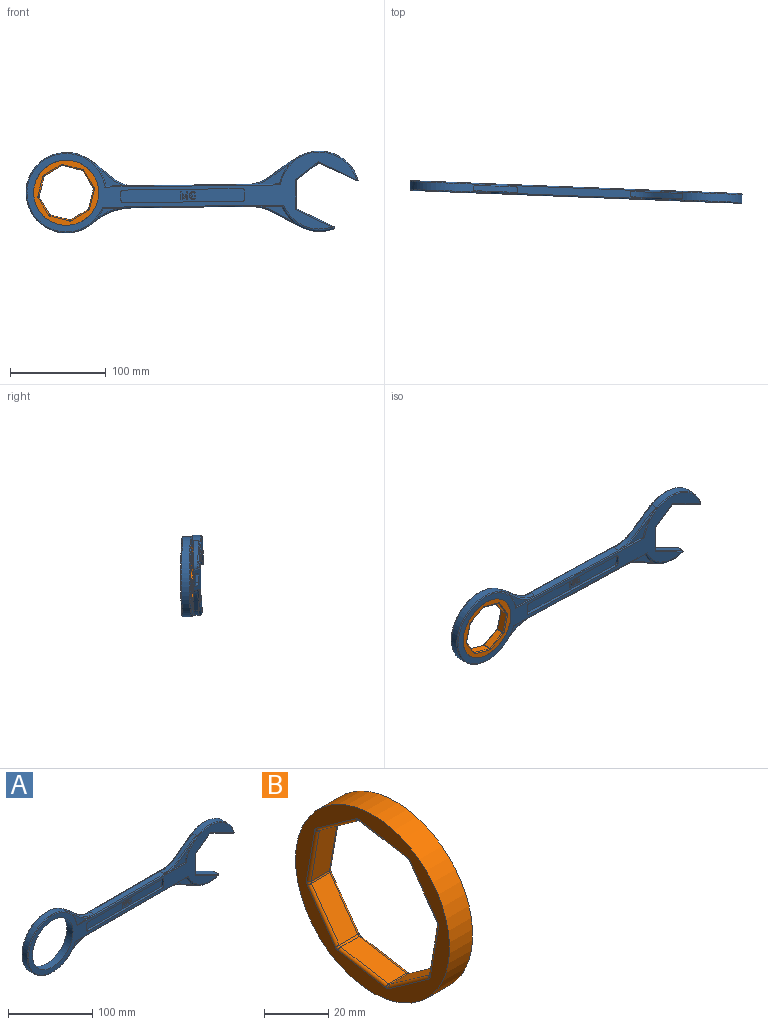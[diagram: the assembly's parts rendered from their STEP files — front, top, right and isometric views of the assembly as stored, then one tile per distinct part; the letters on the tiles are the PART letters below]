
ASSEMBLY  parts=2 mates=1
PART A: 202 faces, bbox 353.1x10.8x92.8 mm
  f0: plane 146.75x8.45mm, normal (0,0,-1), area 986mm2, adj f6,f9,f10,f187,f190,f191,f194,f196
  f1: plane 1.62x0.64mm, normal (0,0,-1), area 0.3mm2, adj f5,f162,f196
  f2: plane 1.62x0.64mm, normal (0,0,-1), area 0.3mm2, adj f4,f161,f194
  f3: plane 137.92x8.42mm, normal (0,0,1), area 976.1mm2, adj f179,f182,f183,f184,f192,f193,f195,f197
  f4: cylinder r=41.91mm len=21.18mm, axis (0,1,0), area 40.1mm2, adj f2,f6,f8,f9,f161
  f5: cylinder r=41.91mm len=21.18mm, axis (0,1,0), area 40.1mm2, adj f1,f6,f7,f10,f162
  f6: extruded ~54.46x21.18mm, area 331.4mm2, adj f0,f4,f5,f9,f10,f11
  f7: plane 34.13x16.45mm, normal (0,-1,0), area 139.1mm2, adj f5,f10,f196
  f8: plane 34.12x16.45mm, normal (0,1,0), area 139.1mm2, adj f4,f9,f194
  f9: bspline ~61.81x25.48mm, area 97mm2, adj f0,f4,f6,f8
  f10: bspline ~57.96x23.23mm, area 97mm2, adj f0,f5,f6,f7
  f11: cylinder r=41.91mm len=36.16mm, axis (0,1,0), area 190.7mm2, adj f6,f161,f162,f169
  f12: cylinder r=41.91mm len=69.07mm, axis (0,1,0), area 633.7mm2, adj f174,f175,f178,f179,f182,f183
  f13: plane 0.9x0.64mm, normal (1,0,0), area 0.6mm2, adj f14,f27,f128,f160
  f14: plane 2.67x0.64mm, normal (0,0,-1), area 1.7mm2, adj f13,f15,f128,f160
  f15: plane 3.12x0.64mm, normal (-1,0,0), area 2mm2, adj f14,f16,f128,f160
  f16: extruded ~0.64x0.56mm, area 0.5mm2, adj f15,f17,f128,f160
  f17: extruded ~0.66x0.64mm, area 0.5mm2, adj f16,f18,f128,f160
  f18: extruded ~0.71x0.64mm, area 0.5mm2, adj f17,f19,f128,f160
  f19: extruded ~0.73x0.64mm, area 0.5mm2, adj f18,f20,f128,f160
  f20: plane 0.64x0.01mm, normal (0,0,1), area 0mm2, adj f19,f21,f128,f160
  f21: plane 0.96x0.64mm, normal (1,0,0), area 0.6mm2, adj f20,f22,f128,f160
  f22: extruded ~0.64x0.32mm, area 0.2mm2, adj f21,f23,f128,f160
  f23: extruded ~0.64x0.39mm, area 0.3mm2, adj f22,f24,f128,f160
  f24: extruded ~0.64x0.38mm, area 0.3mm2, adj f23,f25,f128,f160
  f25: extruded ~0.64x0.27mm, area 0.2mm2, adj f24,f26,f128,f160
  f26: plane 1.99x0.64mm, normal (1,0,0), area 1.3mm2, adj f25,f27,f128,f160
  f27: plane 1.37x0.64mm, normal (0,0,1), area 0.9mm2, adj f13,f26,f128,f160
  f28: extruded ~1.24x0.64mm, area 0.9mm2, adj f29,f45,f128,f158
  f29: extruded ~1.67x0.64mm, area 1.1mm2, adj f28,f30,f128,f158
  f30: extruded ~1.67x0.64mm, area 1.1mm2, adj f29,f31,f128,f158
  f31: extruded ~1.24x0.64mm, area 0.9mm2, adj f30,f32,f128,f158
  f32: extruded ~0.92x0.8mm, area 0.8mm2, adj f31,f33,f128,f158
  f33: extruded ~1.16x0.64mm, area 0.8mm2, adj f32,f34,f128,f158
  f34: plane 1.09x0.64mm, normal (-1,0,0), area 0.7mm2, adj f33,f35,f128,f158
  f35: extruded ~0.64x0.61mm, area 0.4mm2, adj f34,f36,f128,f158
  f36: extruded ~0.64x0.57mm, area 0.5mm2, adj f35,f37,f128,f158
  f37: extruded ~0.89x0.64mm, area 0.6mm2, adj f36,f38,f128,f158
  f38: extruded ~1.23x0.64mm, area 0.8mm2, adj f37,f39,f128,f158
  f39: extruded ~1.25x0.64mm, area 0.8mm2, adj f38,f40,f128,f158
  f40: extruded ~0.92x0.64mm, area 0.6mm2, adj f39,f41,f128,f158
  f41: extruded ~0.64x0.62mm, area 0.5mm2, adj f40,f42,f128,f158
  f42: extruded ~0.64x0.61mm, area 0.4mm2, adj f41,f43,f128,f158
  f43: plane 1x0.64mm, normal (-1,0,0), area 0.6mm2, adj f42,f44,f128,f158
  f44: extruded ~1.16x0.64mm, area 0.8mm2, adj f43,f45,f128,f158
  f45: extruded ~0.92x0.81mm, area 0.8mm2, adj f28,f44,f128,f158
  f46: extruded ~1.02x0.66mm, area 0.8mm2, adj f47,f53,f128,f156
  f47: plane 0.91x0.81mm, normal (-0.66,0,0.75), area 0.8mm2, adj f46,f48,f128,f156
  f48: extruded ~0.64x0.6mm, area 0.5mm2, adj f47,f49,f128,f156
  f49: extruded ~0.7x0.64mm, area 0.5mm2, adj f48,f50,f128,f156
  f50: plane 0.64x0.04mm, normal (0,0,1), area 0mm2, adj f49,f51,f128,f156
  f51: plane 1.08x0.64mm, normal (1,0,0), area 0.7mm2, adj f50,f52,f128,f156
  f52: plane 0.64x0.01mm, normal (0,0,-1), area 0mm2, adj f51,f53,f128,f156
  f53: extruded ~1.23x0.64mm, area 0.8mm2, adj f46,f52,f128,f156
  f54: plane 2x0.64mm, normal (1,0,0), area 1.3mm2, adj f55,f61,f128,f154
  f55: plane 5x2.17mm, normal (0.92,0,-0.4), area 3.5mm2, adj f54,f56,f128,f154
  f56: plane 1.33x0.64mm, normal (0,0,-1), area 0.8mm2, adj f55,f57,f128,f154
  f57: plane 8.06x0.64mm, normal (-1,0,0), area 5.1mm2, adj f56,f58,f128,f154
  f58: plane 1.33x0.64mm, normal (0,0,1), area 0.8mm2, adj f57,f59,f128,f154
  f59: plane 5.55x0.64mm, normal (1,0,0), area 3.5mm2, adj f58,f60,f128,f154
  f60: plane 4.48x1.8mm, normal (-0.93,0,0.37), area 3.1mm2, adj f59,f61,f128,f154
  f61: plane 0.64x0.36mm, normal (0,0,1), area 0.2mm2, adj f54,f60,f128,f154
  f62: plane 1.34x0.64mm, normal (0,0,1), area 0.8mm2, adj f63,f69,f128,f152
  f63: plane 8.06x0.64mm, normal (1,0,0), area 5.1mm2, adj f62,f64,f128,f152
  f64: plane 1.34x0.64mm, normal (0,0,-1), area 0.8mm2, adj f63,f65,f128,f152
  f65: plane 4.97x2.16mm, normal (-0.92,0,-0.4), area 3.4mm2, adj f64,f66,f128,f152
  f66: plane 2.02x0.64mm, normal (-1,0,0), area 1.3mm2, adj f65,f67,f128,f152
  f67: plane 0.64x0.35mm, normal (0,0,1), area 0.2mm2, adj f66,f68,f128,f152
  f68: plane 4.48x1.81mm, normal (0.93,0,0.38), area 3.1mm2, adj f67,f69,f128,f152
  f69: plane 5.55x0.64mm, normal (-1,0,0), area 3.5mm2, adj f62,f68,f128,f152
  f70: plane 0.9x0.64mm, normal (1,0,0), area 0.6mm2, adj f71,f126,f127,f159
  f71: plane 2.67x0.64mm, normal (0,0,-1), area 1.7mm2, adj f70,f72,f127,f159
  f72: plane 3.12x0.64mm, normal (-1,0,0), area 2mm2, adj f71,f73,f127,f159
  f73: extruded ~0.64x0.56mm, area 0.5mm2, adj f72,f74,f127,f159
  f74: extruded ~0.66x0.64mm, area 0.5mm2, adj f73,f75,f127,f159
  f75: extruded ~0.71x0.64mm, area 0.5mm2, adj f74,f76,f127,f159
  f76: extruded ~0.73x0.64mm, area 0.5mm2, adj f75,f77,f127,f159
  f77: plane 0.64x0.01mm, normal (0,0,1), area 0mm2, adj f76,f78,f127,f159
  f78: plane 0.96x0.64mm, normal (1,0,0), area 0.6mm2, adj f77,f79,f127,f159
  f79: extruded ~0.64x0.32mm, area 0.2mm2, adj f78,f80,f127,f159
  f80: extruded ~0.64x0.39mm, area 0.3mm2, adj f79,f81,f127,f159
  f81: extruded ~0.64x0.38mm, area 0.3mm2, adj f80,f82,f127,f159
  f82: extruded ~0.64x0.27mm, area 0.2mm2, adj f81,f83,f127,f159
  f83: plane 1.99x0.64mm, normal (1,0,0), area 1.3mm2, adj f82,f126,f127,f159
  f84: extruded ~1.24x0.64mm, area 0.9mm2, adj f85,f122,f127,f157
  f85: extruded ~1.67x0.64mm, area 1.1mm2, adj f84,f86,f127,f157
  f86: extruded ~1.67x0.64mm, area 1.1mm2, adj f85,f87,f127,f157
  f87: extruded ~1.24x0.64mm, area 0.9mm2, adj f86,f88,f127,f157
  f88: extruded ~0.92x0.8mm, area 0.8mm2, adj f87,f89,f127,f157
  f89: extruded ~1.16x0.64mm, area 0.8mm2, adj f88,f90,f127,f157
  f90: plane 1.09x0.64mm, normal (-1,0,0), area 0.7mm2, adj f89,f91,f127,f157
  f91: extruded ~0.64x0.61mm, area 0.4mm2, adj f90,f92,f127,f157
  f92: extruded ~0.64x0.57mm, area 0.5mm2, adj f91,f93,f127,f157
  f93: extruded ~0.89x0.64mm, area 0.6mm2, adj f92,f94,f127,f157
  f94: extruded ~1.23x0.64mm, area 0.8mm2, adj f93,f95,f127,f157
  f95: extruded ~1.25x0.64mm, area 0.8mm2, adj f94,f96,f127,f157
  f96: extruded ~0.92x0.64mm, area 0.6mm2, adj f95,f97,f127,f157
  f97: extruded ~0.64x0.62mm, area 0.5mm2, adj f96,f98,f127,f157
  f98: extruded ~0.64x0.61mm, area 0.4mm2, adj f97,f99,f127,f157
  f99: plane 1x0.64mm, normal (-1,0,0), area 0.6mm2, adj f98,f100,f127,f157
  f100: extruded ~1.16x0.64mm, area 0.8mm2, adj f99,f122,f127,f157
  f101: extruded ~1.02x0.66mm, area 0.8mm2, adj f102,f123,f127,f155
  f102: plane 0.91x0.81mm, normal (-0.66,0,0.75), area 0.8mm2, adj f101,f103,f127,f155
  f103: extruded ~0.64x0.6mm, area 0.5mm2, adj f102,f104,f127,f155
  f104: extruded ~0.7x0.64mm, area 0.5mm2, adj f103,f105,f127,f155
  f105: plane 0.64x0.04mm, normal (0,0,1), area 0mm2, adj f104,f106,f127,f155
  f106: plane 1.08x0.64mm, normal (1,0,0), area 0.7mm2, adj f105,f107,f127,f155
  f107: plane 0.64x0.01mm, normal (0,0,-1), area 0mm2, adj f106,f123,f127,f155
  f108: plane 2x0.64mm, normal (1,0,0), area 1.3mm2, adj f109,f124,f127,f153
  f109: plane 5x2.17mm, normal (0.92,0,-0.4), area 3.5mm2, adj f108,f110,f127,f153
  f110: plane 1.33x0.64mm, normal (0,0,-1), area 0.8mm2, adj f109,f111,f127,f153
  f111: plane 8.06x0.64mm, normal (-1,0,0), area 5.1mm2, adj f110,f112,f127,f153
  f112: plane 1.33x0.64mm, normal (0,0,1), area 0.8mm2, adj f111,f113,f127,f153
  f113: plane 5.55x0.64mm, normal (1,0,0), area 3.5mm2, adj f112,f114,f127,f153
  f114: plane 4.48x1.8mm, normal (-0.93,0,0.37), area 3.1mm2, adj f113,f124,f127,f153
  f115: plane 1.34x0.64mm, normal (0,0,1), area 0.8mm2, adj f116,f125,f127,f151
  f116: plane 8.06x0.64mm, normal (1,0,0), area 5.1mm2, adj f115,f117,f127,f151
  f117: plane 1.34x0.64mm, normal (0,0,-1), area 0.8mm2, adj f116,f118,f127,f151
  f118: plane 4.97x2.16mm, normal (-0.92,0,-0.4), area 3.4mm2, adj f117,f119,f127,f151
  f119: plane 2.02x0.64mm, normal (-1,0,0), area 1.3mm2, adj f118,f120,f127,f151
  f120: plane 0.64x0.35mm, normal (0,0,1), area 0.2mm2, adj f119,f121,f127,f151
  f121: plane 4.48x1.81mm, normal (0.93,0,0.38), area 3.1mm2, adj f120,f125,f127,f151
  f122: extruded ~0.92x0.81mm, area 0.8mm2, adj f84,f100,f127,f157
  f123: extruded ~1.23x0.64mm, area 0.8mm2, adj f101,f107,f127,f155
  f124: plane 0.64x0.36mm, normal (0,0,1), area 0.2mm2, adj f108,f114,f127,f153
  f125: plane 5.55x0.64mm, normal (-1,0,0), area 3.5mm2, adj f115,f121,f127,f151
  f126: plane 1.37x0.64mm, normal (0,0,1), area 0.9mm2, adj f70,f83,f127,f159
  f127: plane 129.12x13.21mm, normal (0,-1,0), area 1646.9mm2, adj f70,f71,f72,f73,f74,f75,f76,f77
  f128: plane 129.12x13.21mm, normal (0,1,0), area 1646.9mm2, adj f13,f14,f15,f16,f17,f18,f19,f20
  f129: plane 124.04x3.18mm, normal (0,0,1), area 393.8mm2, adj f127,f133,f136,f149
  f130: plane 8.13x3.18mm, normal (-1,0,0), area 25.8mm2, adj f127,f135,f136,f149
  f131: plane 124.04x3.18mm, normal (0,0,-1), area 393.8mm2, adj f127,f134,f135,f149
  f132: plane 8.13x3.18mm, normal (1,0,0), area 25.8mm2, adj f127,f133,f134,f149
  f133: cylinder r=2.54mm len=3.18mm, axis (0,1,0), area 12.7mm2, adj f127,f129,f132,f149
  f134: cylinder r=2.54mm len=3.18mm, axis (0,1,0), area 12.7mm2, adj f127,f131,f132,f149
  f135: cylinder r=2.54mm len=3.18mm, axis (0,1,0), area 12.7mm2, adj f127,f130,f131,f149
  f136: cylinder r=2.54mm len=3.18mm, axis (0,1,0), area 12.7mm2, adj f127,f129,f130,f149
  f137: plane 124.04x3.18mm, normal (0,0,1), area 393.8mm2, adj f128,f138,f148,f150
  f138: cylinder r=2.54mm len=3.18mm, axis (0,1,0), area 12.7mm2, adj f128,f137,f139,f150
  f139: plane 8.13x3.18mm, normal (1,0,0), area 25.8mm2, adj f128,f138,f140,f150
  f140: cylinder r=2.54mm len=3.18mm, axis (0,1,0), area 12.7mm2, adj f128,f139,f141,f150
  f141: plane 124.04x3.18mm, normal (0,0,-1), area 393.8mm2, adj f128,f140,f142,f150
  f142: cylinder r=2.54mm len=3.18mm, axis (0,1,0), area 12.7mm2, adj f128,f141,f143,f150
  f143: plane 8.13x3.18mm, normal (-1,0,0), area 25.8mm2, adj f128,f142,f148,f150
  f144: plane 38.78x19.45mm, normal (0.45,0,0.89), area 351.3mm2, adj f145,f166,f167,f169,f171,f173
  f145: plane 29.84x8.13mm, normal (1,0,0), area 242.5mm2, adj f144,f146,f165,f172
  f146: plane 23.92x17.84mm, normal (0.6,0,-0.8), area 242.5mm2, adj f145,f147,f164,f170
  f147: plane 38.78x19.45mm, normal (-0.45,0,-0.89), area 352.7mm2, adj f146,f163,f168,f178
  f148: cylinder r=2.54mm len=3.18mm, axis (0,1,0), area 12.7mm2, adj f128,f137,f143,f150
  f149: plane 343.98x81.98mm, normal (0,-1,0), area 5715.1mm2, adj f129,f130,f131,f132,f133,f134,f135,f136
  f150: plane 343.98x81.98mm, normal (0,1,0), area 5715.1mm2, adj f137,f138,f139,f140,f141,f142,f143,f148
  f151: plane 8.06x3.5mm, normal (0,-1,0), area 16.5mm2, adj f115,f116,f117,f118,f119,f120,f121,f125
  f152: plane 8.06x3.5mm, normal (0,1,0), area 16.5mm2, adj f62,f63,f64,f65,f66,f67,f68,f69
  f153: plane 8.06x3.5mm, normal (0,-1,0), area 16.4mm2, adj f108,f109,f110,f111,f112,f113,f114,f124
  f154: plane 8.06x3.5mm, normal (0,1,0), area 16.4mm2, adj f54,f55,f56,f57,f58,f59,f60,f61
  f155: plane 2.25x1.68mm, normal (0,-1,0), area 2.3mm2, adj f101,f102,f103,f104,f105,f106,f107,f123
  f156: plane 2.25x1.68mm, normal (0,1,0), area 2.3mm2, adj f46,f47,f48,f49,f50,f51,f52,f53
  f157: plane 8.18x2.9mm, normal (0,-1,0), area 11.3mm2, adj f84,f85,f86,f87,f88,f89,f90,f91
  f158: plane 8.18x2.9mm, normal (0,1,0), area 11.3mm2, adj f28,f29,f30,f31,f32,f33,f34,f35
  f159: plane 4.21x2.67mm, normal (0,-1,0), area 7.3mm2, adj f70,f71,f72,f73,f74,f75,f76,f77
  f160: plane 4.21x2.67mm, normal (0,1,0), area 7.3mm2, adj f13,f14,f15,f16,f17,f18,f19,f20
  f161: torus R=39.37mm, axis (0,-1,0), area 253.2mm2, adj f2,f4,f11,f150,f171,f194
  f162: torus R=39.37mm, axis (0,-1,0), area 253.2mm2, adj f1,f5,f11,f149,f167,f196
  f163: cylinder r=1.02mm len=39.8mm, axis (-0.89,0,0.45), area 69.7mm2, adj f147,f149,f164,f176
  f164: cylinder r=1.02mm len=25.44mm, axis (-0.8,0,-0.6), area 48.5mm2, adj f146,f149,f163,f165
  f165: cylinder r=1.02mm len=30.97mm, axis (0,0,-1), area 48.5mm2, adj f145,f149,f164,f166
  f166: cylinder r=1.02mm len=37.92mm, axis (0.89,0,-0.45), area 66.4mm2, adj f144,f149,f165,f167
  f167: bspline ~4.58x3.53mm, area 8.3mm2, adj f144,f162,f166,f169
  f168: cylinder r=1.02mm len=39.8mm, axis (0.89,0,-0.45), area 69.7mm2, adj f147,f150,f170,f177
  f169: cylinder r=1.02mm len=5.08mm, axis (0,1,0), area 11.9mm2, adj f11,f144,f167,f171
  f170: cylinder r=1.02mm len=25.44mm, axis (0.8,0,0.6), area 48.5mm2, adj f146,f150,f168,f172
  f171: bspline ~4.58x3.54mm, area 8.3mm2, adj f144,f161,f169,f173
  f172: cylinder r=1.02mm len=30.97mm, axis (0,0,1), area 48.5mm2, adj f145,f150,f170,f173
  f173: cylinder r=1.02mm len=37.92mm, axis (-0.89,0,0.45), area 66.4mm2, adj f144,f150,f171,f172
  f174: torus R=40.89mm, axis (0,-1,0), area 177.5mm2, adj f12,f149,f176,f180,f197
  f175: torus R=40.89mm, axis (0,-1,0), area 177.5mm2, adj f12,f150,f177,f181,f195
  f176: sphere r=1.02mm, area 1.6mm2, adj f163,f174,f178
  f177: sphere r=1.02mm, area 1.6mm2, adj f168,f175,f178
  f178: cylinder r=1.02mm len=8.13mm, axis (0,1,0), area 19.1mm2, adj f12,f147,f176,f177
  f179: extruded ~54.46x27.96mm, area 348.4mm2, adj f3,f12,f182,f183
  f180: plane 35.96x22.36mm, normal (0,-1,0), area 189mm2, adj f174,f183,f197
  f181: plane 35.96x22.36mm, normal (0,1,0), area 189mm2, adj f175,f182,f195
  f182: bspline ~57.62x29.94mm, area 104.6mm2, adj f3,f12,f179,f181
  f183: bspline ~57.62x29.94mm, area 104.6mm2, adj f3,f12,f179,f180
  f184: extruded ~45.41x27.23mm, area 302.3mm2, adj f3,f192,f193,f198
  f185: plane 29.57x20.81mm, normal (0,-1,0), area 139.8mm2, adj f193,f197,f201
  f186: plane 29.57x20.81mm, normal (0,1,0), area 139.8mm2, adj f192,f195,f200
  f187: extruded ~44.78x16.54mm, area 273.1mm2, adj f0,f190,f191,f198
  f188: plane 23.13x10.1mm, normal (0,-1,0), area 59.5mm2, adj f191,f196,f201
  f189: plane 23.13x10.1mm, normal (0,1,0), area 59.5mm2, adj f190,f194,f200
  f190: bspline ~47.31x18.69mm, area 74mm2, adj f0,f187,f189,f198
  f191: bspline ~49.81x18.66mm, area 74mm2, adj f0,f187,f188,f198
  f192: bspline ~47.67x29.28mm, area 90.2mm2, adj f3,f184,f186,f198
  f193: bspline ~47.58x29.28mm, area 90.2mm2, adj f3,f184,f185,f198
  f194: cylinder r=1.02mm len=189.14mm, axis (1,0,0), area 299.9mm2, adj f0,f2,f8,f150,f161,f189,f200
  f195: cylinder r=1.02mm len=182.96mm, axis (-1,0,0), area 290.6mm2, adj f3,f150,f175,f181,f186,f200
  f196: cylinder r=1.02mm len=189.14mm, axis (-1,0,0), area 299.9mm2, adj f0,f1,f7,f149,f162,f188,f201
  f197: cylinder r=1.02mm len=182.96mm, axis (1,0,0), area 290.6mm2, adj f3,f149,f174,f180,f185,f201
  f198: cylinder r=41.91mm len=83.82mm, axis (0,1,0), area 1535.7mm2, adj f184,f187,f190,f191,f192,f193,f200,f201
  f199: cylinder r=33.93mm len=67.85mm, axis (0,1,0), area 2165.8mm2, adj f149,f150
  f200: torus R=40.89mm, axis (0,-1,0), area 380.6mm2, adj f150,f186,f189,f194,f195,f198
  f201: torus R=40.89mm, axis (0,-1,0), area 380.6mm2, adj f149,f185,f188,f196,f197,f198
PART B: 51 faces, bbox 10.2x67.8x67.8 mm
  f0: plane 17.35x12.27mm, normal (0,-0.58,-0.82), area 172.7mm2, adj f39,f44,f47,f50
  f1: plane 20.95x8.13mm, normal (0,-0.99,-0.17), area 172.7mm2, adj f36,f45,f46,f50
  f2: plane 17.35x12.27mm, normal (0,-0.82,0.58), area 172.7mm2, adj f26,f35,f36,f37
  f3: plane 20.95x8.13mm, normal (0,-0.17,0.99), area 172.7mm2, adj f16,f25,f26,f27
  f4: plane 17.35x12.27mm, normal (0,0.58,0.82), area 172.7mm2, adj f11,f15,f16,f17
  f5: plane 20.95x8.13mm, normal (0,0.99,0.17), area 172.7mm2, adj f11,f14,f18,f19
  f6: plane 17.35x12.27mm, normal (0,0.82,-0.58), area 172.7mm2, adj f19,f24,f28,f29
  f7: plane 20.95x8.13mm, normal (0,0.17,-0.99), area 172.7mm2, adj f29,f34,f38,f39
  f8: cylinder r=33.92mm len=67.84mm, axis (-1,0,0), area 2165.5mm2, adj f9,f10
  f9: plane 67.84x67.84mm, normal (1,0,0), area 1075.7mm2, adj f8,f12,f14,f15,f20,f21,f24,f25
  f10: plane 67.84x67.84mm, normal (-1,0,0), area 1075.7mm2, adj f8,f13,f17,f18,f22,f23,f27,f28
  f11: cylinder r=1.02mm len=8.13mm, axis (1,0,0), area 6.5mm2, adj f4,f5,f12,f13
  f12: torus R=2.03mm, axis (1,0,0), area 1.7mm2, adj f9,f11,f14,f15
  f13: torus R=2.03mm, axis (1,0,0), area 1.7mm2, adj f10,f11,f17,f18
  f14: cylinder r=1.02mm len=21.12mm, axis (0,0.17,-0.99), area 33.9mm2, adj f5,f9,f12,f20
  f15: cylinder r=1.02mm len=17.94mm, axis (0,0.82,-0.58), area 33.9mm2, adj f4,f9,f12,f21
  f16: cylinder r=1.02mm len=8.13mm, axis (1,0,0), area 6.5mm2, adj f3,f4,f21,f22
  f17: cylinder r=1.02mm len=17.94mm, axis (0,-0.82,0.58), area 33.9mm2, adj f4,f10,f13,f22
  f18: cylinder r=1.02mm len=21.12mm, axis (0,-0.17,0.99), area 33.9mm2, adj f5,f10,f13,f23
  f19: cylinder r=1.02mm len=8.13mm, axis (1,0,0), area 6.5mm2, adj f5,f6,f20,f23
  f20: torus R=2.03mm, axis (1,0,0), area 1.7mm2, adj f9,f14,f19,f24
  f21: torus R=2.03mm, axis (1,0,0), area 1.7mm2, adj f9,f15,f16,f25
  f22: torus R=2.03mm, axis (1,0,0), area 1.7mm2, adj f10,f16,f17,f27
  f23: torus R=2.03mm, axis (1,0,0), area 1.7mm2, adj f10,f18,f19,f28
  f24: cylinder r=1.02mm len=17.94mm, axis (0,-0.58,-0.82), area 33.9mm2, adj f6,f9,f20,f30
  f25: cylinder r=1.02mm len=21.12mm, axis (0,0.99,0.17), area 33.9mm2, adj f3,f9,f21,f31
  f26: cylinder r=1.02mm len=8.13mm, axis (1,0,0), area 6.5mm2, adj f2,f3,f31,f32
  f27: cylinder r=1.02mm len=21.12mm, axis (0,-0.99,-0.17), area 33.9mm2, adj f3,f10,f22,f32
  f28: cylinder r=1.02mm len=17.94mm, axis (0,0.58,0.82), area 33.9mm2, adj f6,f10,f23,f33
  f29: cylinder r=1.02mm len=8.13mm, axis (1,0,0), area 6.5mm2, adj f6,f7,f30,f33
  f30: torus R=2.03mm, axis (1,0,0), area 1.7mm2, adj f9,f24,f29,f34
  f31: torus R=2.03mm, axis (1,0,0), area 1.7mm2, adj f9,f25,f26,f35
  f32: torus R=2.03mm, axis (1,0,0), area 1.7mm2, adj f10,f26,f27,f37
  f33: torus R=2.03mm, axis (1,0,0), area 1.7mm2, adj f10,f28,f29,f38
  f34: cylinder r=1.02mm len=21.12mm, axis (0,-0.99,-0.17), area 33.9mm2, adj f7,f9,f30,f40
  f35: cylinder r=1.02mm len=17.94mm, axis (0,0.58,0.82), area 33.9mm2, adj f2,f9,f31,f41
  f36: cylinder r=1.02mm len=8.13mm, axis (1,0,0), area 6.5mm2, adj f1,f2,f41,f42
  f37: cylinder r=1.02mm len=17.94mm, axis (0,-0.58,-0.82), area 33.9mm2, adj f2,f10,f32,f42
  f38: cylinder r=1.02mm len=21.12mm, axis (0,0.99,0.17), area 33.9mm2, adj f7,f10,f33,f43
  f39: cylinder r=1.02mm len=8.13mm, axis (1,0,0), area 6.5mm2, adj f0,f7,f40,f43
  f40: torus R=2.03mm, axis (1,0,0), area 1.7mm2, adj f9,f34,f39,f44
  f41: torus R=2.03mm, axis (1,0,0), area 1.7mm2, adj f9,f35,f36,f45
  f42: torus R=2.03mm, axis (1,0,0), area 1.7mm2, adj f10,f36,f37,f46
  f43: torus R=2.03mm, axis (1,0,0), area 1.7mm2, adj f10,f38,f39,f47
  f44: cylinder r=1.02mm len=17.94mm, axis (0,-0.82,0.58), area 33.9mm2, adj f0,f9,f40,f48
  f45: cylinder r=1.02mm len=21.12mm, axis (0,-0.17,0.99), area 33.9mm2, adj f1,f9,f41,f48
  f46: cylinder r=1.02mm len=21.12mm, axis (0,0.17,-0.99), area 33.9mm2, adj f1,f10,f42,f49
  f47: cylinder r=1.02mm len=17.94mm, axis (0,0.82,-0.58), area 33.9mm2, adj f0,f10,f43,f49
  f48: torus R=2.03mm, axis (1,0,0), area 1.7mm2, adj f9,f44,f45,f50
  f49: torus R=2.03mm, axis (1,0,0), area 1.7mm2, adj f10,f46,f47,f50
  f50: cylinder r=1.02mm len=8.13mm, axis (1,0,0), area 6.5mm2, adj f0,f1,f48,f49
PLACE A rot(axis=(0.01,-0.3,-0.95),2.3deg) t=(-97,-62.14,-36.05)mm
PLACE B rot(axis=(0.7,0.67,0.25),150.8deg) t=(-130.79,-60.86,52.78)mm
MATE revolute B.f8 <-> A.f198  axis (-0.04,-1,0) through (-147.89,-60.16,-4.6)mm
